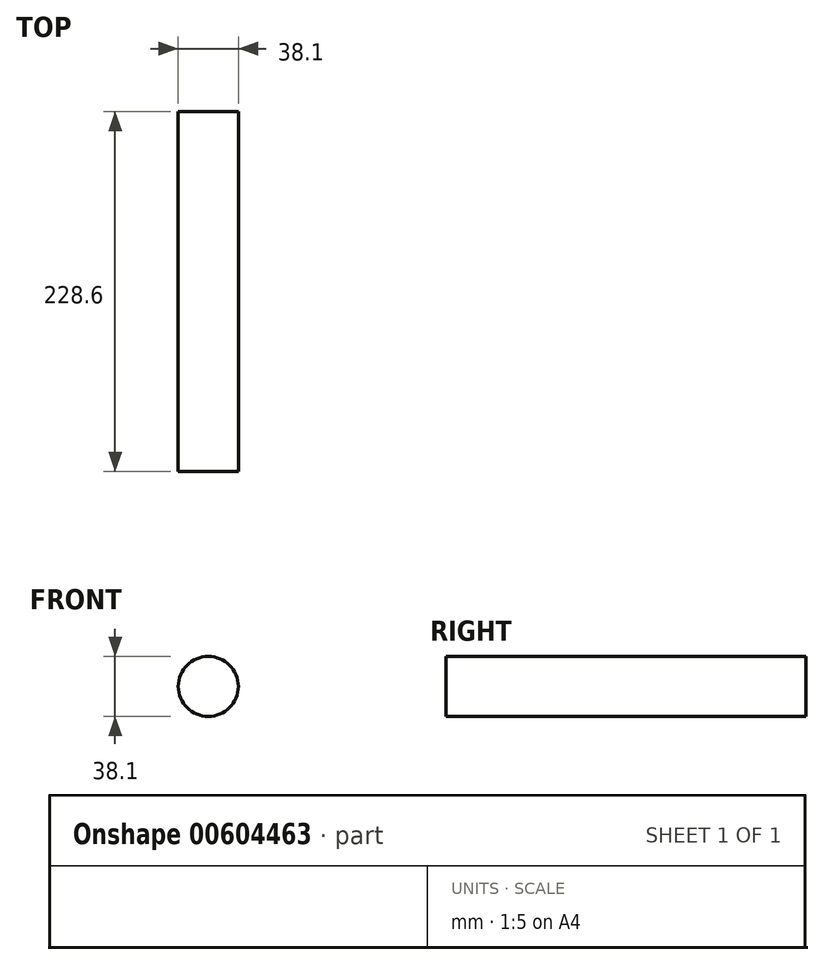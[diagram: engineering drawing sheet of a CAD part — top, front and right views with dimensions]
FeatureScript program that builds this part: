
annotation { "Feature Type Name" : "Feature", "Feature Type Description" : "" }
export const myFeature = defineFeature(function(context is Context, id is Id, definition is map)
    precondition{}
    {
        {
            var Q0;
            Q0=qCreatedBy(makeId("Front.planeOp"),FACE);
            var sketch = newSketch(context, id + "F0", { "sketchPlane" : qUnion([Q0])});
            skCircle(sketch, "E0", {"center": v(0, 0) * mm, "radius": 19.05 * mm});
            skSolve(sketch);
        }
        {
            var Q0;
            Q0=makeQuery(id+"F0.imprint","IMPRINT",FACE,{"disambiguationData":[TD([[makeQuery(id+"F0.imprint","IMPRINT",EDGE,{"derivedFrom":sQuery(id+"F0.wireOp",EDGE,"E0")}),1.0]])]});
            extrude(context, id + "F1", {"entities" : qUnion([Q0]), "depth" : 228.6 * mm, "offsetDistance" : 25.4 * mm});
        }
        {
            var Q0;
            Q0=makeQuery(id+"F1.opExtrude","CAP_FACE",FACE,{"disambiguationData":[OSD([sQuery(id+"F0.wireOp",EDGE,"E0")])],"isStart":false});
            var sketch = newSketch(context, id + "F2", { "sketchPlane" : qUnion([Q0])});
            skCircle(sketch, "E1", {"center": v(0, 0) * mm, "radius": 19.73 * mm});
            skSolve(sketch);
        }
        {
            var Q0;
            Q0=sQuery(id+"F2.wireOp",EDGE,"E1");
            extrude(context, id + "F3", {"bodyType" : ToolBodyType.SURFACE, "surfaceEntities" : qUnion([Q0]), "depth" : -228.6 * mm, "offsetDistance" : 25.4 * mm});
        }
    });
